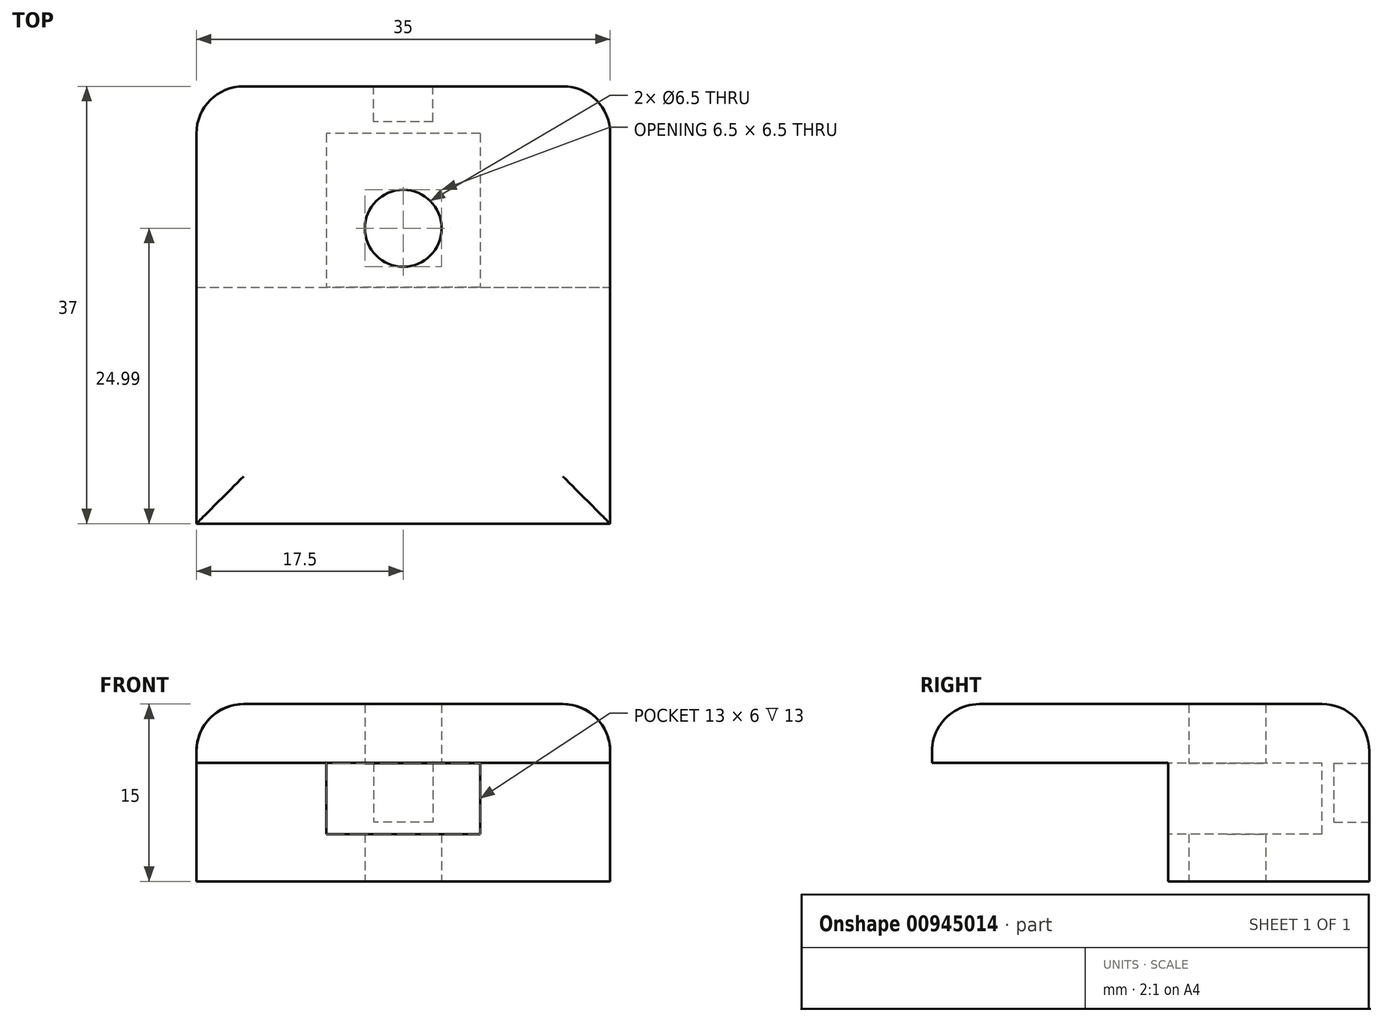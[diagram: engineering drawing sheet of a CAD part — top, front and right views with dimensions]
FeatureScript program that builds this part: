
annotation { "Feature Type Name" : "Feature", "Feature Type Description" : "" }
export const myFeature = defineFeature(function(context is Context, id is Id, definition is map)
    precondition{}
    {
        {
            var Q0;
            Q0=qCreatedBy(makeId("Front.planeOp"),FACE);
            var sketch = newSketch(context, id + "F0", { "sketchPlane" : qUnion([Q0])});
            skLineSegment(sketch, "E0.bottom", {"start": v(-22.33, 3.43) * mm, "end": v(12.67, 3.43) * mm});
            skLineSegment(sketch, "E0.top", {"start": v(-22.33, -11.57) * mm, "end": v(12.67, -11.57) * mm});
            skLineSegment(sketch, "E0.left", {"start": v(-22.33, 3.43) * mm, "end": v(-22.33, -11.57) * mm});
            skLineSegment(sketch, "E0.right", {"start": v(12.67, 3.43) * mm, "end": v(12.67, -11.57) * mm});
            skSolve(sketch);
        }
        {
            var Q0;
            Q0=makeQuery(id+"F0.imprint","IMPRINT",FACE,{"disambiguationData":[TD([[makeQuery(id+"F0.imprint","IMPRINT",EDGE,{"derivedFrom":sQuery(id+"F0.wireOp",EDGE,"E0.bottom")}),-1.0]])]});
            extrude(context, id + "F1", {"entities" : qUnion([Q0]), "depth" : 17 * mm, "offsetDistance" : 25 * mm});
        }
        {
            var Q0;
            Q0=makeQuery(id+"F1.opExtrude","CAP_FACE",FACE,{"disambiguationData":[OSD([sQuery(id+"F0.wireOp",EDGE,"E0.bottom"),sQuery(id+"F0.wireOp",EDGE,"E0.top"),sQuery(id+"F0.wireOp",EDGE,"E0.left"),sQuery(id+"F0.wireOp",EDGE,"E0.right")])],"isStart":false});
            var sketch = newSketch(context, id + "F2", { "sketchPlane" : qUnion([Q0])});
            skLineSegment(sketch, "E1.bottom", {"start": v(-22.33, 3.43) * mm, "end": v(12.67, 3.43) * mm});
            skLineSegment(sketch, "E1.top", {"start": v(-22.33, 3.43) * mm, "end": v(12.67, 3.43) * mm});
            skLineSegment(sketch, "E1.left", {"start": v(-22.33, 3.43) * mm, "end": v(-22.33, 3.43) * mm});
            skLineSegment(sketch, "E1.right", {"start": v(12.67, 3.43) * mm, "end": v(12.67, 3.43) * mm});
            skLineSegment(sketch, "E2.top", {"start": v(-22.33, -1.56) * mm, "end": v(12.67, -1.56) * mm});
            skLineSegment(sketch, "E2.left", {"start": v(-22.33, 3.43) * mm, "end": v(-22.33, -1.56) * mm});
            skLineSegment(sketch, "E2.right", {"start": v(12.67, 3.43) * mm, "end": v(12.67, -1.56) * mm});
            skSolve(sketch);
        }
        {
            var Q0;
            Q0=makeQuery(id+"F2.imprint","IMPRINT",FACE,{"disambiguationData":[TD([[makeQuery(id+"F2.imprint","IMPRINT",EDGE,{"derivedFrom":sQuery(id+"F2.wireOp",EDGE,"E1.bottom")}),-1.0]])]});
            extrude(context, id + "F3", {"entities" : qUnion([Q0]), "operationType" : NewBodyOperationType.ADD, "depth" : 20 * mm, "offsetDistance" : 25 * mm});
        }
        {
            var Q0;
            Q0=makeQuery(id+"F1.opExtrude","CAP_FACE",FACE,{"disambiguationData":[OSD([sQuery(id+"F0.wireOp",EDGE,"E0.bottom"),sQuery(id+"F0.wireOp",EDGE,"E0.top"),sQuery(id+"F0.wireOp",EDGE,"E0.left"),sQuery(id+"F0.wireOp",EDGE,"E0.right")])],"isStart":false});
            var sketch = newSketch(context, id + "F4", { "sketchPlane" : qUnion([Q0])});
            skLineSegment(sketch, "E3", {"start": v(-4.83, -11.57) * mm, "end": v(-4.83, -7.57) * mm});
            skLineSegment(sketch, "E4", {"start": v(-4.83, -7.57) * mm, "end": v(1.67, -7.57) * mm});
            skLineSegment(sketch, "E5", {"start": v(1.67, -7.57) * mm, "end": v(1.67, -1.57) * mm});
            skLineSegment(sketch, "E6.MirrorCS", {"start": v(-4.83, -7.57) * mm, "end": v(-11.33, -7.57) * mm});
            skLineSegment(sketch, "E7.bottom", {"start": v(-11.33, -7.57) * mm, "end": v(1.67, -7.57) * mm});
            skLineSegment(sketch, "E8.top", {"start": v(-11.33, -1.57) * mm, "end": v(1.67, -1.57) * mm});
            skLineSegment(sketch, "E8.left", {"start": v(-11.33, -7.57) * mm, "end": v(-11.33, -1.57) * mm});
            skSolve(sketch);
        }
        {
            var Q0;
            Q0=makeQuery(id+"F4.imprint","IMPRINT",FACE,{"disambiguationData":[TD([[makeQuery(id+"F4.imprint","IMPRINT",EDGE,{"derivedFrom":sQuery(id+"F4.wireOp",EDGE,"E4")}),1.0]])]});
            extrude(context, id + "F5", {"entities" : qUnion([Q0]), "operationType" : NewBodyOperationType.REMOVE, "oppositeDirection" : true, "depth" : 13 * mm, "offsetDistance" : 25 * mm});
        }
        {
            var Q0;
            Q0=makeQuery(id+"F1.opExtrude","SWEPT_FACE",FACE,{"disambiguationData":[OSD([sQuery(id+"F0.wireOp",EDGE,"E0.top")])]});
            var sketch = newSketch(context, id + "F6", { "sketchPlane" : qUnion([Q0])});
            skLineSegment(sketch, "E9", {"start": v(-4.83, 17) * mm, "end": v(-4.83, 12) * mm});
            skCircle(sketch, "E10", {"center": v(-4.83, 12) * mm, "radius": 3.25 * mm});
            skSolve(sketch);
        }
        {
            var Q0;
            Q0=makeQuery(id+"F6.imprint","IMPRINT",FACE,{"disambiguationData":[TD([[makeQuery(id+"F6.imprint","IMPRINT",EDGE,{"derivedFrom":sQuery(id+"F6.wireOp",EDGE,"E10")}),1.0]])]});
            extrude(context, id + "F7", {"entities" : qUnion([Q0]), "operationType" : NewBodyOperationType.REMOVE, "oppositeDirection" : true, "depth" : 25 * mm, "offsetDistance" : 25 * mm});
        }
        {
            var Q0;
            Q0=makeQuery(id+"F1.opExtrude","CAP_FACE",FACE,{"disambiguationData":[OSD([sQuery(id+"F0.wireOp",EDGE,"E0.bottom"),sQuery(id+"F0.wireOp",EDGE,"E0.top"),sQuery(id+"F0.wireOp",EDGE,"E0.left"),sQuery(id+"F0.wireOp",EDGE,"E0.right")])],"isStart":true});
            var sketch = newSketch(context, id + "F8", { "sketchPlane" : qUnion([Q0])});
            skLineSegment(sketch, "E11.bottom", {"start": v(2.33, -1.57) * mm, "end": v(7.33, -1.57) * mm});
            skLineSegment(sketch, "E11.top", {"start": v(2.33, -6.57) * mm, "end": v(7.33, -6.57) * mm});
            skLineSegment(sketch, "E11.left", {"start": v(2.33, -1.57) * mm, "end": v(2.33, -6.57) * mm});
            skLineSegment(sketch, "E11.right", {"start": v(7.33, -1.57) * mm, "end": v(7.33, -6.57) * mm});
            skPoint(sketch, "E11.middle", {"position": v(4.83, -4.07) * mm});
            skPoint(sketch, "E11.middle.positionSnap0", {"position": v(4.83, 3.43) * mm});
            skPoint(sketch, "E11.middle.positionSnap1", {"position": v(-12.67, -4.07) * mm});
            skPoint(sketch, "E11.centerSnap0", {"position": v(4.83, 3.43) * mm});
            skPoint(sketch, "E11.centerSnap1", {"position": v(-12.67, -4.07) * mm});
            skSolve(sketch);
        }
        {
            var Q0;
            Q0 = qSketchRegion(id + "F8", true);
            var Q1;
            Q1=makeQuery(id+"F8.imprint","IMPRINT",FACE,{"disambiguationData":[TD([[makeQuery(id+"F8.imprint","IMPRINT",EDGE,{"derivedFrom":sQuery(id+"F8.wireOp",EDGE,"E11.bottom")}),-1.0]])]});
            extrude(context, id + "F9", {"entities" : qUnion([Q0, Q1]), "operationType" : NewBodyOperationType.REMOVE, "oppositeDirection" : true, "depth" : 3 * mm, "offsetDistance" : 25 * mm});
        }
        {
            var Q0;
            Q0=makeQuery(id+"F3.boolean.opBoolean","MERGE",EDGE,{"derivedFrom":[makeQuery(id+"F1.opExtrude","SWEPT_EDGE",EDGE,{"disambiguationData":[OSD([sQuery(id+"F0.wireOp",EDGE,"E0.bottom"),sQuery(id+"F0.wireOp",EDGE,"E0.right")])]}),makeQuery(id+"F3.opExtrude","SWEPT_EDGE",EDGE,{"disambiguationData":[OSD([sQuery(id+"F2.wireOp",EDGE,"E1.bottom"),sQuery(id+"F2.wireOp",EDGE,"E2.right")])]})]});
            var Q1;
            Q1=makeQuery(id+"F3.opExtrude","CAP_EDGE",EDGE,{"disambiguationData":[OSD([sQuery(id+"F2.wireOp",EDGE,"E1.bottom")])],"isStart":false});
            var Q2;
            Q2=makeQuery(id+"F3.boolean.opBoolean","MERGE",EDGE,{"derivedFrom":[makeQuery(id+"F1.opExtrude","SWEPT_EDGE",EDGE,{"disambiguationData":[OSD([sQuery(id+"F0.wireOp",EDGE,"E0.bottom"),sQuery(id+"F0.wireOp",EDGE,"E0.left")])]}),makeQuery(id+"F3.opExtrude","SWEPT_EDGE",EDGE,{"disambiguationData":[OSD([sQuery(id+"F2.wireOp",EDGE,"E1.bottom"),sQuery(id+"F2.wireOp",EDGE,"E2.left")])]})]});
            var Q3;
            Q3=makeQuery(id+"F1.opExtrude","CAP_EDGE",EDGE,{"disambiguationData":[OSD([sQuery(id+"F0.wireOp",EDGE,"E0.bottom")])],"isStart":true});
            var Q4;
            Q4=makeQuery(id+"F1.opExtrude","CAP_EDGE",EDGE,{"disambiguationData":[OSD([sQuery(id+"F0.wireOp",EDGE,"E0.left")])],"isStart":true});
            var Q5;
            Q5=makeQuery(id+"F1.opExtrude","CAP_EDGE",EDGE,{"disambiguationData":[OSD([sQuery(id+"F0.wireOp",EDGE,"E0.right")])],"isStart":true});
            fillet(context, id + "F10", {"entities" : qUnion([Q0, Q1, Q2, Q3, Q4, Q5]), "radius" : 4 * mm, "tangentPropagation" : true, "allowEdgeOverflow" : false});
        }
    });
